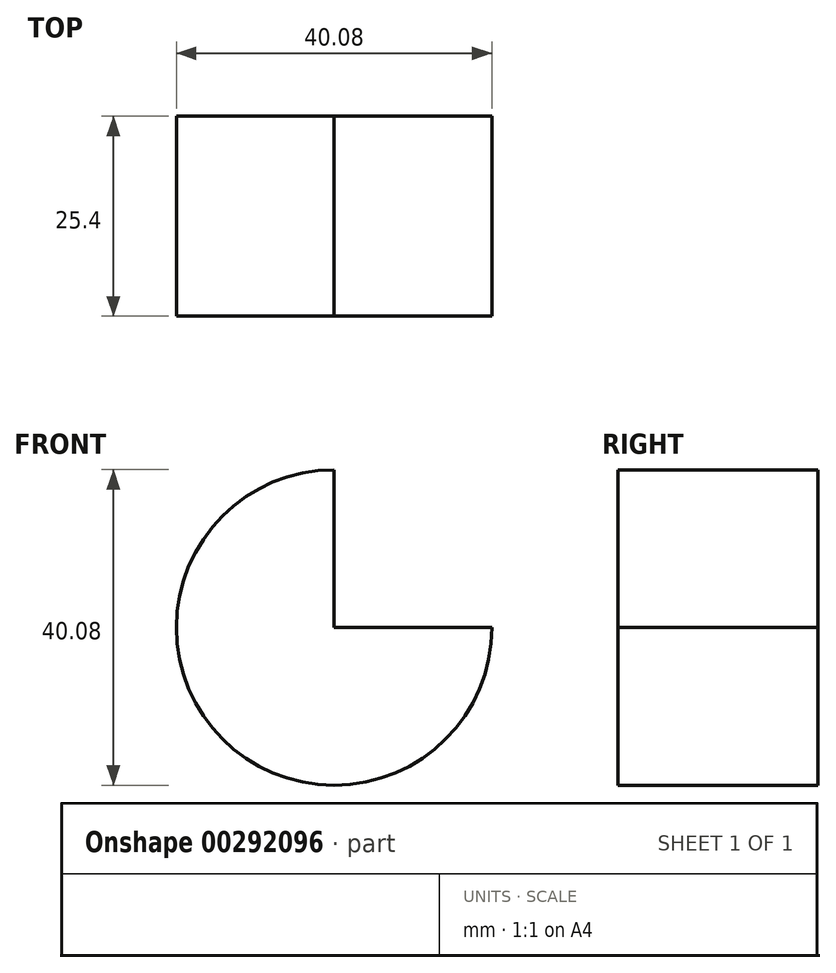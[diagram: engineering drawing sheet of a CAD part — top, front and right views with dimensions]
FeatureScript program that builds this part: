
annotation { "Feature Type Name" : "Feature", "Feature Type Description" : "" }
export const myFeature = defineFeature(function(context is Context, id is Id, definition is map)
    precondition{}
    {
        {
            var Q0;
            Q0=qCreatedBy(makeId("Front.planeOp"),FACE);
            var sketch = newSketch(context, id + "F0", { "sketchPlane" : qUnion([Q0])});
            skCircle(sketch, "E0", {"center": v(0, 0) * mm, "radius": 26.56 * mm});
            skCircle(sketch, "E1", {"center": v(0, -72.75) * mm, "radius": 20.04 * mm});
            skCircle(sketch, "E2", {"center": v(0, 84.86) * mm, "radius": 27.2 * mm});
            skCircle(sketch, "E3", {"center": v(103.32, -72.75) * mm, "radius": 19.98 * mm});
            skLineSegment(sketch, "E4", {"start": v(0, 84.86) * mm, "end": v(0, 0) * mm});
            skLineSegment(sketch, "E5", {"start": v(0, -72.75) * mm, "end": v(0, 0) * mm});
            skLineSegment(sketch, "E6", {"start": v(0, -72.75) * mm, "end": v(103.32, -72.75) * mm});
            skLineSegment(sketch, "E7", {"start": v(-26.56, 78.96) * mm, "end": v(-26.56, 0) * mm});
            skLineSegment(sketch, "E8", {"start": v(26.75, 89.83) * mm, "end": v(26.75, 0) * mm});
            skLineSegment(sketch, "E9", {"start": v(-26.56, 0) * mm, "end": v(-20.04, -72.75) * mm});
            skLineSegment(sketch, "E10", {"start": v(0, -92.8) * mm, "end": v(103.32, -92.74) * mm});
            skLineSegment(sketch, "E11", {"start": v(26.75, 0) * mm, "end": v(26.75, -40.26) * mm});
            skLineSegment(sketch, "E12", {"start": v(103.32, -52.77) * mm, "end": v(40.6, -52.77) * mm});
            skArc(sketch, "E13", {"start": v(26.75, -40.26) * mm, "mid": v(41.82, -52.2) * mm, "end": v(39.83, -33.07) * mm});
            skSolve(sketch);
        }
        {
            var Q0;
            Q0=makeQuery(id+"F0.imprint","IMPRINT",FACE,{"disambiguationData":[TD([[makeQuery(id+"F0.imprint","IMPRINT",EDGE,{"derivedFrom":sQuery(id+"F0.wireOp",EDGE,"E1")}),1.0]])]});
            extrude(context, id + "F1", {"entities" : qUnion([Q0]), "depth" : 25.4 * mm});
        }
    });
